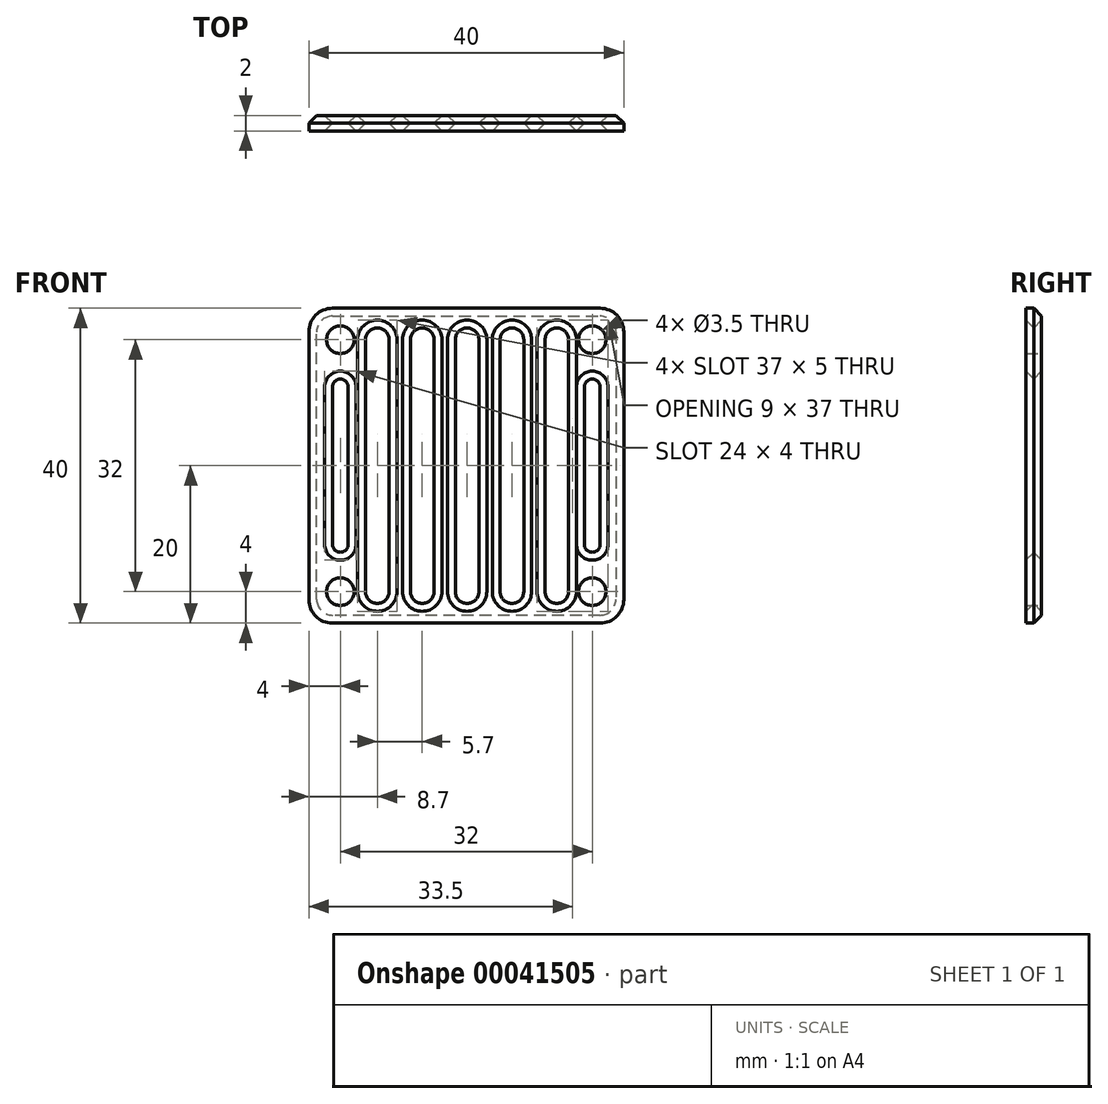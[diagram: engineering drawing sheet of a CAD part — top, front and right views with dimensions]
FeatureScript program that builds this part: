
annotation { "Feature Type Name" : "Feature", "Feature Type Description" : "" }
export const myFeature = defineFeature(function(context is Context, id is Id, definition is map)
    precondition{}
    {
        {
            var Q0;
            Q0=qCreatedBy(makeId("Front.planeOp"),FACE);
            var sketch = newSketch(context, id + "F0", { "sketchPlane" : qUnion([Q0])});
            skLineSegment(sketch, "E0.rect.bottom", {"start": v(17, 20) * mm, "end": v(-17, 20) * mm});
            skLineSegment(sketch, "E0.rect.top", {"start": v(17, -20) * mm, "end": v(-17, -20) * mm});
            skLineSegment(sketch, "E0.rect.left", {"start": v(20, 17) * mm, "end": v(20, -17) * mm});
            skLineSegment(sketch, "E0.rect.right", {"start": v(-20, 17) * mm, "end": v(-20, -17) * mm});
            skPoint(sketch, "E0.rect.middle", {"position": v(0, 0) * mm});
            skCircle(sketch, "E1", {"center": v(16, 16) * mm, "radius": 1.75 * mm});
            skCircle(sketch, "E2.0.1.0", {"center": v(16, -16) * mm, "radius": 1.75 * mm});
            skCircle(sketch, "E2.1.0.0", {"center": v(-16, 16) * mm, "radius": 1.75 * mm});
            skCircle(sketch, "E2.1.1.0", {"center": v(-16, -16) * mm, "radius": 1.75 * mm});
            skLineSegment(sketch, "E2.direction1", {"start": v(16, 16) * mm, "end": v(-16, 16) * mm, "construction": true});
            skLineSegment(sketch, "E2.direction2", {"start": v(16, 16) * mm, "end": v(16, -16) * mm, "construction": true});
            skPoint(sketch, "E3.visualSharp", {"position": v(20, 20) * mm});
            skArc(sketch, "E3.filletArc", {"start": v(20, 17) * mm, "mid": v(19.12, 19.12) * mm, "end": v(17, 20) * mm});
            skPoint(sketch, "E4.visualSharp", {"position": v(-20, 20) * mm});
            skArc(sketch, "E4.filletArc", {"start": v(-17, 20) * mm, "mid": v(-19.12, 19.12) * mm, "end": v(-20, 17) * mm});
            skPoint(sketch, "E5.visualSharp", {"position": v(-20, -20) * mm});
            skArc(sketch, "E5.filletArc", {"start": v(-20, -17) * mm, "mid": v(-19.12, -19.12) * mm, "end": v(-17, -20) * mm});
            skPoint(sketch, "E6.visualSharp", {"position": v(20, -20) * mm});
            skArc(sketch, "E6.filletArc", {"start": v(17, -20) * mm, "mid": v(19.12, -19.12) * mm, "end": v(20, -17) * mm});
            skLineSegment(sketch, "E7.left", {"start": v(13, 16) * mm, "end": v(13, -16) * mm});
            skLineSegment(sketch, "E7.right", {"start": v(10, 16) * mm, "end": v(10, -16) * mm});
            skArc(sketch, "E8", {"start": v(13, 16) * mm, "mid": v(11.5, 17.5) * mm, "end": v(10, 16) * mm});
            skArc(sketch, "E9", {"start": v(10, -16) * mm, "mid": v(11.5, -17.5) * mm, "end": v(13, -16) * mm});
            skArc(sketch, "E10.1.0.0", {"start": v(4.3, -16) * mm, "mid": v(5.8, -17.5) * mm, "end": v(7.3, -16) * mm});
            skLineSegment(sketch, "E10.1.0.1", {"start": v(4.3, 16) * mm, "end": v(4.3, -16) * mm});
            skLineSegment(sketch, "E10.1.0.2", {"start": v(7.3, 16) * mm, "end": v(7.3, -16) * mm});
            skArc(sketch, "E10.1.0.3", {"start": v(7.3, 16) * mm, "mid": v(5.8, 17.5) * mm, "end": v(4.3, 16) * mm});
            skArc(sketch, "E10.2.0.0", {"start": v(-1.4, -16) * mm, "mid": v(0.1, -17.5) * mm, "end": v(1.6, -16) * mm});
            skLineSegment(sketch, "E10.2.0.1", {"start": v(-1.4, 16) * mm, "end": v(-1.4, -16) * mm});
            skLineSegment(sketch, "E10.2.0.2", {"start": v(1.6, 16) * mm, "end": v(1.6, -16) * mm});
            skArc(sketch, "E10.2.0.3", {"start": v(1.6, 16) * mm, "mid": v(0.1, 17.5) * mm, "end": v(-1.4, 16) * mm});
            skArc(sketch, "E10.3.0.0", {"start": v(-7.1, -16) * mm, "mid": v(-5.6, -17.5) * mm, "end": v(-4.1, -16) * mm});
            skLineSegment(sketch, "E10.3.0.1", {"start": v(-7.1, 16) * mm, "end": v(-7.1, -16) * mm});
            skLineSegment(sketch, "E10.3.0.2", {"start": v(-4.1, 16) * mm, "end": v(-4.1, -16) * mm});
            skArc(sketch, "E10.3.0.3", {"start": v(-4.1, 16) * mm, "mid": v(-5.6, 17.5) * mm, "end": v(-7.1, 16) * mm});
            skArc(sketch, "E10.4.0.0", {"start": v(-12.8, -16) * mm, "mid": v(-11.3, -17.5) * mm, "end": v(-9.8, -16) * mm});
            skLineSegment(sketch, "E10.4.0.1", {"start": v(-12.8, 16) * mm, "end": v(-12.8, -16) * mm});
            skLineSegment(sketch, "E10.4.0.2", {"start": v(-9.8, 16) * mm, "end": v(-9.8, -16) * mm});
            skArc(sketch, "E10.4.0.3", {"start": v(-9.8, 16) * mm, "mid": v(-11.3, 17.5) * mm, "end": v(-12.8, 16) * mm});
            skLineSegment(sketch, "E10.direction1", {"start": v(10, -16) * mm, "end": v(4.3, -16) * mm, "construction": true});
            skLineSegment(sketch, "E11.rect.left", {"start": v(15, 10) * mm, "end": v(15, -10) * mm});
            skLineSegment(sketch, "E11.rect.right", {"start": v(17, 10) * mm, "end": v(17, -10) * mm});
            skPoint(sketch, "E11.rect.middle", {"position": v(16, 0) * mm});
            skArc(sketch, "E12", {"start": v(17, 10) * mm, "mid": v(16, 11) * mm, "end": v(15, 10) * mm});
            skArc(sketch, "E13", {"start": v(15, -10) * mm, "mid": v(16, -11) * mm, "end": v(17, -10) * mm});
            skPoint(sketch, "E14.1.0.0", {"position": v(-16, 0) * mm});
            skArc(sketch, "E14.1.0.1", {"start": v(-15, 10) * mm, "mid": v(-16, 11) * mm, "end": v(-17, 10) * mm});
            skLineSegment(sketch, "E14.1.0.2", {"start": v(-15, 10) * mm, "end": v(-15, -10) * mm});
            skLineSegment(sketch, "E14.1.0.3", {"start": v(-17, 10) * mm, "end": v(-17, -10) * mm});
            skArc(sketch, "E14.1.0.4", {"start": v(-17, -10) * mm, "mid": v(-16, -11) * mm, "end": v(-15, -10) * mm});
            skLineSegment(sketch, "E14.direction1", {"start": v(16, 0) * mm, "end": v(-16, 0) * mm, "construction": true});
            skSolve(sketch);
        }
        {
            var Q0;
            Q0=makeQuery(id+"F0.imprint","IMPRINT",FACE,{"disambiguationData":[TD([[makeQuery(id+"F0.imprint","IMPRINT",EDGE,{"derivedFrom":sQuery(id+"F0.wireOp",EDGE,"E0.rect.bottom")}),1.0]])]});
            extrude(context, id + "F1", {"entities" : qUnion([Q0]), "depth" : 2 * mm});
        }
        {
            var Q0;
            Q0=makeQuery(id+"F1.opExtrude","CAP_EDGE",EDGE,{"disambiguationData":[OSD([sQuery(id+"F0.wireOp",EDGE,"E11.rect.right")])],"isStart":true});
            var Q1;
            Q1=makeQuery(id+"F1.opExtrude","CAP_EDGE",EDGE,{"disambiguationData":[OSD([sQuery(id+"F0.wireOp",EDGE,"E11.rect.left")])],"isStart":true});
            var Q2;
            Q2=makeQuery(id+"F1.opExtrude","CAP_EDGE",EDGE,{"disambiguationData":[OSD([sQuery(id+"F0.wireOp",EDGE,"E12")])],"isStart":true});
            var Q3;
            Q3=makeQuery(id+"F1.opExtrude","CAP_EDGE",EDGE,{"disambiguationData":[OSD([sQuery(id+"F0.wireOp",EDGE,"E13")])],"isStart":true});
            var Q4;
            Q4=makeQuery(id+"F1.opExtrude","CAP_EDGE",EDGE,{"disambiguationData":[OSD([sQuery(id+"F0.wireOp",EDGE,"E7.left")])],"isStart":true});
            var Q5;
            Q5=makeQuery(id+"F1.opExtrude","CAP_EDGE",EDGE,{"disambiguationData":[OSD([sQuery(id+"F0.wireOp",EDGE,"E10.1.0.2")])],"isStart":true});
            var Q6;
            Q6=makeQuery(id+"F1.opExtrude","CAP_EDGE",EDGE,{"disambiguationData":[OSD([sQuery(id+"F0.wireOp",EDGE,"E10.2.0.2")])],"isStart":true});
            var Q7;
            Q7=makeQuery(id+"F1.opExtrude","CAP_EDGE",EDGE,{"disambiguationData":[OSD([sQuery(id+"F0.wireOp",EDGE,"E10.3.0.2")])],"isStart":true});
            var Q8;
            Q8=makeQuery(id+"F1.opExtrude","CAP_EDGE",EDGE,{"disambiguationData":[OSD([sQuery(id+"F0.wireOp",EDGE,"E10.4.0.2")])],"isStart":true});
            var Q9;
            Q9=makeQuery(id+"F1.opExtrude","CAP_EDGE",EDGE,{"disambiguationData":[OSD([sQuery(id+"F0.wireOp",EDGE,"E14.1.0.2")])],"isStart":true});
            var Q10;
            Q10=makeQuery(id+"F1.opExtrude","CAP_EDGE",EDGE,{"disambiguationData":[OSD([sQuery(id+"F0.wireOp",EDGE,"E10.4.0.2")])],"isStart":false});
            var Q11;
            Q11=makeQuery(id+"F1.opExtrude","CAP_EDGE",EDGE,{"disambiguationData":[OSD([sQuery(id+"F0.wireOp",EDGE,"E14.1.0.2")])],"isStart":false});
            var Q12;
            Q12=makeQuery(id+"F1.opExtrude","CAP_EDGE",EDGE,{"disambiguationData":[OSD([sQuery(id+"F0.wireOp",EDGE,"E10.3.0.2")])],"isStart":false});
            var Q13;
            Q13=makeQuery(id+"F1.opExtrude","CAP_EDGE",EDGE,{"disambiguationData":[OSD([sQuery(id+"F0.wireOp",EDGE,"E10.2.0.2")])],"isStart":false});
            var Q14;
            Q14=makeQuery(id+"F1.opExtrude","CAP_EDGE",EDGE,{"disambiguationData":[OSD([sQuery(id+"F0.wireOp",EDGE,"E10.1.0.2")])],"isStart":false});
            var Q15;
            Q15=makeQuery(id+"F1.opExtrude","CAP_EDGE",EDGE,{"disambiguationData":[OSD([sQuery(id+"F0.wireOp",EDGE,"E7.left")])],"isStart":false});
            var Q16;
            Q16=makeQuery(id+"F1.opExtrude","CAP_EDGE",EDGE,{"disambiguationData":[OSD([sQuery(id+"F0.wireOp",EDGE,"E11.rect.right")])],"isStart":false});
            var Q17;
            Q17=makeQuery(id+"F1.opExtrude","CAP_EDGE",EDGE,{"disambiguationData":[OSD([sQuery(id+"F0.wireOp",EDGE,"E0.rect.right")])],"isStart":true});
            chamfer(context, id + "F2", {"entities" : qUnion([Q0, Q1, Q2, Q3, Q4, Q5, Q6, Q7, Q8, Q9, Q10, Q11, Q12, Q13, Q14, Q15, Q16, Q17]), "width" : 1 * mm, "tangentPropagation" : true});
        }
    });
